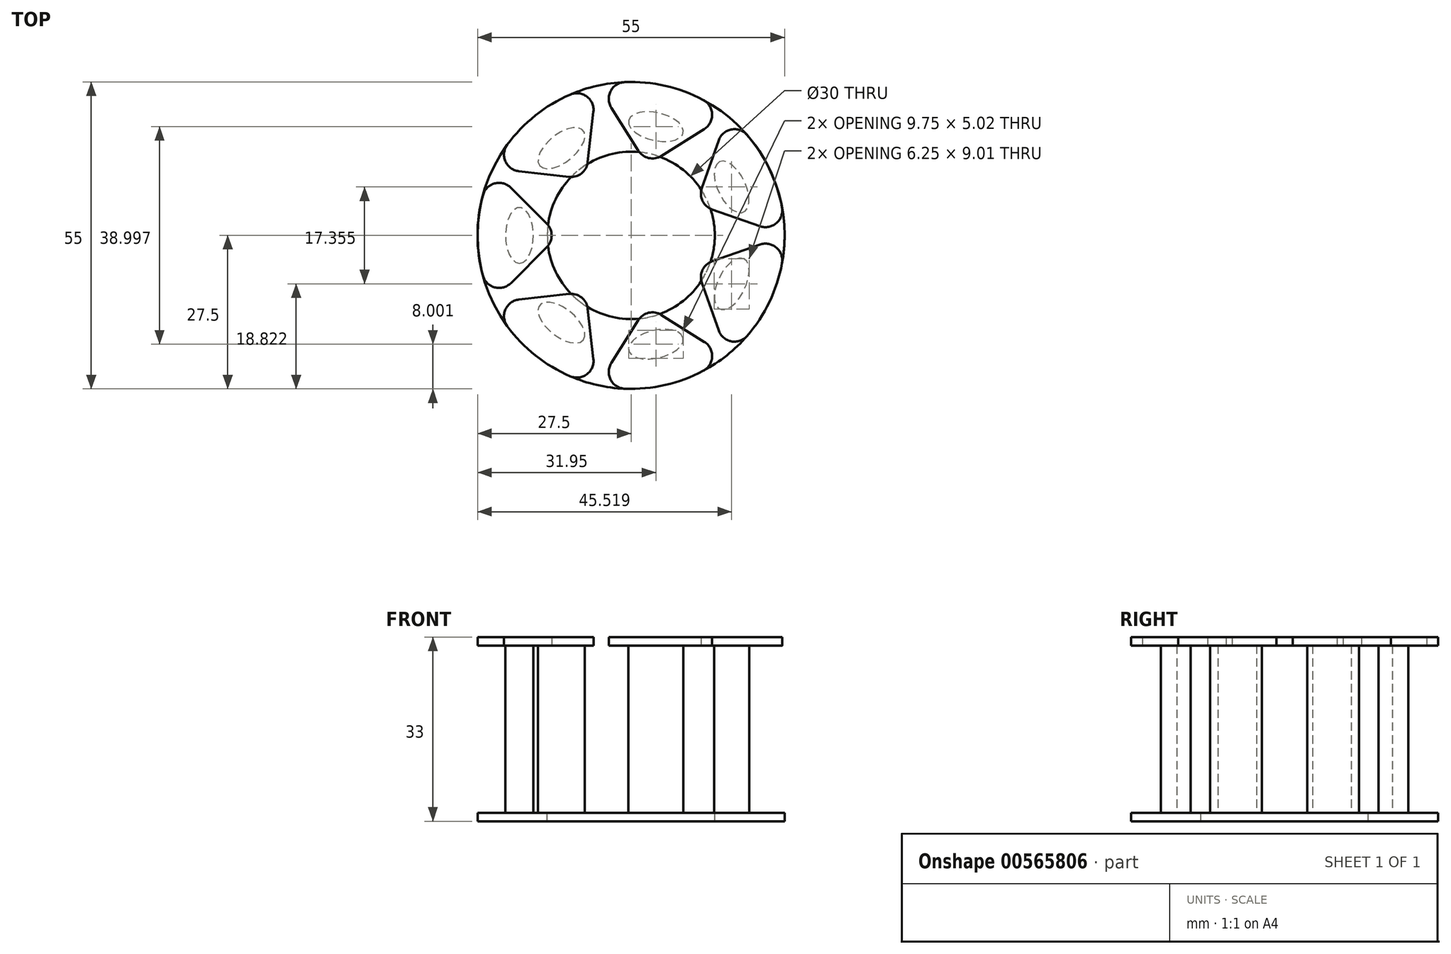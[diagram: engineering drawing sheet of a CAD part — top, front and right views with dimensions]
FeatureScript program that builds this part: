
annotation { "Feature Type Name" : "Feature", "Feature Type Description" : "" }
export const myFeature = defineFeature(function(context is Context, id is Id, definition is map)
    precondition{}
    {
        {
            var Q0;
            Q0=qCreatedBy(makeId("Top.planeOp"),FACE);
            var sketch = newSketch(context, id + "F0", { "sketchPlane" : qUnion([Q0])});
            skCircle(sketch, "E0", {"center": v(0, 0) * mm, "radius": 27.5 * mm});
            skSolve(sketch);
        }
        {
            var Q0;
            Q0 = qSketchRegion(id + "F0", true);
            extrude(context, id + "F1", {"entities" : qUnion([Q0]), "oppositeDirection" : true, "depth" : 1.5 * mm, "offsetDistance" : 25 * mm});
        }
        {
            var Q0;
            Q0=makeQuery(id+"F1.opExtrude","CAP_FACE",FACE,{"disambiguationData":[OSD([sQuery(id+"F0.wireOp",EDGE,"E0")])],"isStart":true});
            var sketch = newSketch(context, id + "F2", { "sketchPlane" : qUnion([Q0])});
            skCircle(sketch, "E1", {"center": v(0, 0) * mm, "radius": 15 * mm});
            skSolve(sketch);
        }
        {
            var Q0;
            Q0=makeQuery(id+"F2.imprint","IMPRINT",FACE,{"disambiguationData":[TD([[makeQuery(id+"F2.imprint","IMPRINT",EDGE,{"derivedFrom":sQuery(id+"F2.wireOp",EDGE,"E1")}),1.0]])]});
            var Q1;
            Q1=makeQuery(id+"F1.opExtrude","CAP_FACE",FACE,{"disambiguationData":[OSD([sQuery(id+"F0.wireOp",EDGE,"E0")])],"isStart":false});
            extrude(context, id + "F3", {"entities" : qUnion([Q0]), "operationType" : NewBodyOperationType.REMOVE, "endBound" : BoundingType.UP_TO_SURFACE, "oppositeDirection" : true, "depth" : 25 * mm, "endBoundEntityFace" : qUnion([Q1]), "offsetDistance" : 25 * mm});
        }
        {
            var Q0;
            Q0=makeQuery(id+"F1.opExtrude","CAP_FACE",FACE,{"disambiguationData":[OSD([sQuery(id+"F0.wireOp",EDGE,"E0")])],"isStart":true});
            var sketch = newSketch(context, id + "F4", { "sketchPlane" : qUnion([Q0])});
            skEllipse(sketch, "E2", {"center": v(-20, 0) * mm, "majorRadius": 5 * mm, "minorRadius": 2.5 * mm, "majorAxis": v(0, -1)});
            skEllipse(sketch, "E3.1.0", {"center": v(-12.47, -15.64) * mm, "majorRadius": 5 * mm, "minorRadius": 2.5 * mm, "majorAxis": v(0.78, -0.62)});
            skEllipse(sketch, "E3.2.0", {"center": v(4.45, -19.5) * mm, "majorRadius": 5 * mm, "minorRadius": 2.5 * mm, "majorAxis": v(0.97, 0.22)});
            skEllipse(sketch, "E3.3.0", {"center": v(18.02, -8.68) * mm, "majorRadius": 5 * mm, "minorRadius": 2.5 * mm, "majorAxis": v(0.43, 0.9)});
            skEllipse(sketch, "E3.4.0", {"center": v(18.02, 8.68) * mm, "majorRadius": 5 * mm, "minorRadius": 2.5 * mm, "majorAxis": v(-0.43, 0.9)});
            skEllipse(sketch, "E3.5.0", {"center": v(4.45, 19.5) * mm, "majorRadius": 5 * mm, "minorRadius": 2.5 * mm, "majorAxis": v(-0.97, 0.22)});
            skEllipse(sketch, "E3.6.0", {"center": v(-12.47, 15.64) * mm, "majorRadius": 5 * mm, "minorRadius": 2.5 * mm, "majorAxis": v(-0.78, -0.62)});
            skPoint(sketch, "E3.center", {"position": v(0, 0) * mm});
            skSolve(sketch);
        }
        {
            var Q0;
            Q0=makeQuery(id+"F4.imprint","IMPRINT",FACE,{"disambiguationData":[TD([[makeQuery(id+"F4.imprint","IMPRINT",EDGE,{"derivedFrom":sQuery(id+"F4.wireOp",EDGE,"E3.1.0")}),1.0]])]});
            var Q1;
            Q1=makeQuery(id+"F4.imprint","IMPRINT",FACE,{"disambiguationData":[TD([[makeQuery(id+"F4.imprint","IMPRINT",EDGE,{"derivedFrom":sQuery(id+"F4.wireOp",EDGE,"E3.2.0")}),1.0]])]});
            var Q2;
            Q2=makeQuery(id+"F4.imprint","IMPRINT",FACE,{"disambiguationData":[TD([[makeQuery(id+"F4.imprint","IMPRINT",EDGE,{"derivedFrom":sQuery(id+"F4.wireOp",EDGE,"E3.3.0")}),1.0]])]});
            var Q3;
            Q3=makeQuery(id+"F4.imprint","IMPRINT",FACE,{"disambiguationData":[TD([[makeQuery(id+"F4.imprint","IMPRINT",EDGE,{"derivedFrom":sQuery(id+"F4.wireOp",EDGE,"E3.4.0")}),1.0]])]});
            var Q4;
            Q4=makeQuery(id+"F4.imprint","IMPRINT",FACE,{"disambiguationData":[TD([[makeQuery(id+"F4.imprint","IMPRINT",EDGE,{"derivedFrom":sQuery(id+"F4.wireOp",EDGE,"E3.5.0")}),1.0]])]});
            var Q5;
            Q5=makeQuery(id+"F4.imprint","IMPRINT",FACE,{"disambiguationData":[TD([[makeQuery(id+"F4.imprint","IMPRINT",EDGE,{"derivedFrom":sQuery(id+"F4.wireOp",EDGE,"E3.6.0")}),1.0]])]});
            var Q6;
            Q6=makeQuery(id+"F4.imprint","IMPRINT",FACE,{"disambiguationData":[TD([[makeQuery(id+"F4.imprint","IMPRINT",EDGE,{"derivedFrom":sQuery(id+"F4.wireOp",EDGE,"E2")}),1.0]])]});
            extrude(context, id + "F5", {"entities" : qUnion([Q0, Q1, Q2, Q3, Q4, Q5, Q6]), "operationType" : NewBodyOperationType.ADD, "depth" : 30 * mm, "offsetDistance" : 25 * mm});
        }
        {
            var Q0;
            Q0=makeQuery(id+"F5.opExtrude","CAP_FACE",FACE,{"disambiguationData":[OSD([sQuery(id+"F4.wireOp",EDGE,"E2")])],"isStart":false});
            var sketch = newSketch(context, id + "F6", { "sketchPlane" : qUnion([Q0])});
            skLineSegment(sketch, "E4", {"start": v(-15.1, 2.12) * mm, "end": v(-21.52, 8.54) * mm});
            skLineSegment(sketch, "E5", {"start": v(-21.52, -8.54) * mm, "end": v(-15.1, -2.12) * mm});
            skArc(sketch, "E6", {"start": v(-26.54, 7.2) * mm, "mid": v(-27.5, 0) * mm, "end": v(-26.54, -7.2) * mm});
            skPoint(sketch, "E7", {"position": v(-22.5, 0) * mm});
            skPoint(sketch, "E8", {"position": v(-17.5, 0) * mm});
            skPoint(sketch, "E9.visualSharp", {"position": v(-24.82, 11.84) * mm});
            skArc(sketch, "E9.filletArc", {"start": v(-21.52, 8.54) * mm, "mid": v(-24.42, 9.32) * mm, "end": v(-26.54, 7.2) * mm});
            skPoint(sketch, "E10.visualSharp", {"position": v(-24.82, -11.84) * mm});
            skArc(sketch, "E10.filletArc", {"start": v(-26.54, -7.2) * mm, "mid": v(-24.42, -9.32) * mm, "end": v(-21.52, -8.54) * mm});
            skPoint(sketch, "E11.visualSharp", {"position": v(-12.98, 0) * mm});
            skArc(sketch, "E11.filletArc", {"start": v(-15.1, -2.12) * mm, "mid": v(-14.22, 0) * mm, "end": v(-15.1, 2.12) * mm});
            skLineSegment(sketch, "E12.1.0", {"start": v(-11.08, -10.49) * mm, "end": v(-20.1, -11.5) * mm});
            skArc(sketch, "E12.1.1", {"start": v(-20.1, -11.5) * mm, "mid": v(-22.5, -13.28) * mm, "end": v(-22.18, -16.26) * mm});
            skArc(sketch, "E12.1.2", {"start": v(-22.18, -16.26) * mm, "mid": v(-17.15, -21.5) * mm, "end": v(-10.91, -25.24) * mm});
            skArc(sketch, "E12.1.3", {"start": v(-10.91, -25.24) * mm, "mid": v(-7.94, -24.9) * mm, "end": v(-6.74, -22.15) * mm});
            skLineSegment(sketch, "E12.1.4", {"start": v(-6.74, -22.15) * mm, "end": v(-7.76, -13.13) * mm});
            skArc(sketch, "E12.1.5", {"start": v(-7.76, -13.13) * mm, "mid": v(-8.87, -11.12) * mm, "end": v(-11.08, -10.49) * mm});
            skLineSegment(sketch, "E12.2.0", {"start": v(1.3, -15.2) * mm, "end": v(-3.54, -22.88) * mm});
            skArc(sketch, "E12.2.1", {"start": v(-3.54, -22.88) * mm, "mid": v(-3.65, -25.88) * mm, "end": v(-1.12, -27.48) * mm});
            skArc(sketch, "E12.2.2", {"start": v(-1.12, -27.48) * mm, "mid": v(6.12, -26.81) * mm, "end": v(12.93, -24.27) * mm});
            skArc(sketch, "E12.2.3", {"start": v(12.93, -24.27) * mm, "mid": v(14.52, -21.73) * mm, "end": v(13.12, -19.08) * mm});
            skLineSegment(sketch, "E12.2.4", {"start": v(13.12, -19.08) * mm, "end": v(5.43, -14.25) * mm});
            skArc(sketch, "E12.2.5", {"start": v(5.43, -14.25) * mm, "mid": v(3.17, -13.87) * mm, "end": v(1.3, -15.2) * mm});
            skLineSegment(sketch, "E12.3.0", {"start": v(12.69, -8.46) * mm, "end": v(15.69, -17.03) * mm});
            skArc(sketch, "E12.3.1", {"start": v(15.69, -17.03) * mm, "mid": v(17.95, -18.99) * mm, "end": v(20.78, -18) * mm});
            skArc(sketch, "E12.3.2", {"start": v(20.78, -18) * mm, "mid": v(24.78, -11.93) * mm, "end": v(27.04, -5.02) * mm});
            skArc(sketch, "E12.3.3", {"start": v(27.04, -5.02) * mm, "mid": v(26.04, -2.2) * mm, "end": v(23.1, -1.64) * mm});
            skLineSegment(sketch, "E12.3.4", {"start": v(23.1, -1.64) * mm, "end": v(14.53, -4.64) * mm});
            skArc(sketch, "E12.3.5", {"start": v(14.53, -4.64) * mm, "mid": v(12.82, -6.17) * mm, "end": v(12.69, -8.46) * mm});
            skLineSegment(sketch, "E12.4.0", {"start": v(14.53, 4.64) * mm, "end": v(23.1, 1.64) * mm});
            skArc(sketch, "E12.4.1", {"start": v(23.1, 1.64) * mm, "mid": v(26.04, 2.2) * mm, "end": v(27.04, 5.02) * mm});
            skArc(sketch, "E12.4.2", {"start": v(27.04, 5.02) * mm, "mid": v(24.78, 11.93) * mm, "end": v(20.78, 18) * mm});
            skArc(sketch, "E12.4.3", {"start": v(20.78, 18) * mm, "mid": v(17.95, 18.99) * mm, "end": v(15.69, 17.03) * mm});
            skLineSegment(sketch, "E12.4.4", {"start": v(15.69, 17.03) * mm, "end": v(12.69, 8.46) * mm});
            skArc(sketch, "E12.4.5", {"start": v(12.69, 8.46) * mm, "mid": v(12.82, 6.17) * mm, "end": v(14.53, 4.64) * mm});
            skLineSegment(sketch, "E12.5.0", {"start": v(5.43, 14.25) * mm, "end": v(13.12, 19.08) * mm});
            skArc(sketch, "E12.5.1", {"start": v(13.12, 19.08) * mm, "mid": v(14.52, 21.73) * mm, "end": v(12.93, 24.27) * mm});
            skArc(sketch, "E12.5.2", {"start": v(12.93, 24.27) * mm, "mid": v(6.12, 26.81) * mm, "end": v(-1.12, 27.48) * mm});
            skArc(sketch, "E12.5.3", {"start": v(-1.12, 27.48) * mm, "mid": v(-3.65, 25.88) * mm, "end": v(-3.54, 22.88) * mm});
            skLineSegment(sketch, "E12.5.4", {"start": v(-3.54, 22.88) * mm, "end": v(1.3, 15.2) * mm});
            skArc(sketch, "E12.5.5", {"start": v(1.3, 15.2) * mm, "mid": v(3.17, 13.87) * mm, "end": v(5.43, 14.25) * mm});
            skLineSegment(sketch, "E12.6.0", {"start": v(-7.76, 13.13) * mm, "end": v(-6.74, 22.15) * mm});
            skArc(sketch, "E12.6.1", {"start": v(-6.74, 22.15) * mm, "mid": v(-7.94, 24.9) * mm, "end": v(-10.91, 25.24) * mm});
            skArc(sketch, "E12.6.2", {"start": v(-10.91, 25.24) * mm, "mid": v(-17.15, 21.5) * mm, "end": v(-22.18, 16.26) * mm});
            skArc(sketch, "E12.6.3", {"start": v(-22.18, 16.26) * mm, "mid": v(-22.5, 13.28) * mm, "end": v(-20.1, 11.5) * mm});
            skLineSegment(sketch, "E12.6.4", {"start": v(-20.1, 11.5) * mm, "end": v(-11.08, 10.49) * mm});
            skArc(sketch, "E12.6.5", {"start": v(-11.08, 10.49) * mm, "mid": v(-8.87, 11.12) * mm, "end": v(-7.76, 13.13) * mm});
            skSolve(sketch);
        }
        {
            var Q0;
            Q0 = qSketchRegion(id + "F6", true);
            extrude(context, id + "F7", {"entities" : qUnion([Q0]), "operationType" : NewBodyOperationType.ADD, "depth" : 1.5 * mm, "offsetDistance" : 25 * mm});
        }
    });
